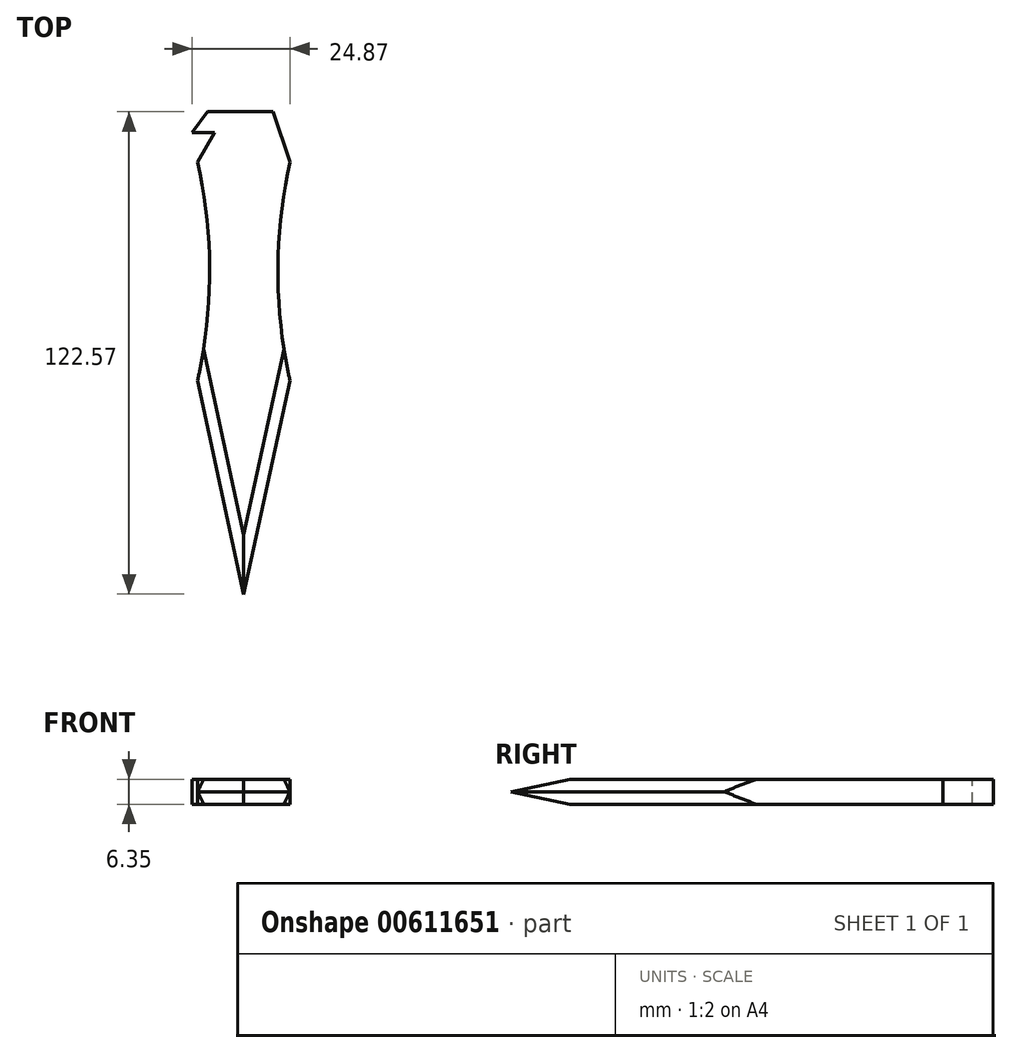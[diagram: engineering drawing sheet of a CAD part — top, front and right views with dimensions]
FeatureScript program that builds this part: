
annotation { "Feature Type Name" : "Feature", "Feature Type Description" : "" }
export const myFeature = defineFeature(function(context is Context, id is Id, definition is map)
    precondition{}
    {
        {
            var Q0;
            Q0=qCreatedBy(makeId("Top.planeOp"),FACE);
            var sketch = newSketch(context, id + "F0", { "sketchPlane" : qUnion([Q0])});
            skLineSegment(sketch, "E0", {"start": v(0, 0) * mm, "end": v(-11.74, 20.33) * mm});
            skLineSegment(sketch, "E1", {"start": v(-63.5, 109.99) * mm, "end": v(63.5, 109.99) * mm});
            skLineSegment(sketch, "E2", {"start": v(63.5, 109.99) * mm, "end": v(0, 0) * mm});
            skLineSegment(sketch, "E3", {"start": v(0, 0) * mm, "end": v(0, 19.44) * mm});
            skLineSegment(sketch, "E4", {"start": v(-60.33, 104.49) * mm, "end": v(-44.45, 109.99) * mm});
            skLineSegment(sketch, "E5.MirrorCS", {"start": v(60.33, 104.49) * mm, "end": v(44.45, 109.99) * mm});
            skLineSegment(sketch, "E6", {"start": v(-44.45, 109.99) * mm, "end": v(0, 63.5) * mm});
            skLineSegment(sketch, "E7", {"start": v(0, 63.5) * mm, "end": v(44.45, 109.99) * mm});
            skPoint(sketch, "E8", {"position": v(-11.74, 20.33) * mm});
            skPoint(sketch, "E9.MirrorP", {"position": v(11.74, 20.33) * mm});
            skLineSegment(sketch, "E10.MirrorCS", {"start": v(11.74, 20.33) * mm, "end": v(0, 29.52) * mm});
            skLineSegment(sketch, "E11.MirrorCS", {"start": v(0, 29.52) * mm, "end": v(-11.74, 20.33) * mm});
            skLineSegment(sketch, "E12", {"start": v(-49.19, 85.2) * mm, "end": v(-43.22, 86.8) * mm});
            skLineSegment(sketch, "E13", {"start": v(-43.22, 86.8) * mm, "end": v(-47.97, 83.1) * mm});
            skLineSegment(sketch, "E14", {"start": v(-35.1, 60.8) * mm, "end": v(-26.52, 63.68) * mm});
            skLineSegment(sketch, "E15", {"start": v(-26.52, 63.68) * mm, "end": v(-33.47, 57.97) * mm});
            skLineSegment(sketch, "E16.trimOffspring", {"start": v(-21.1, 36.55) * mm, "end": v(-33.47, 57.97) * mm});
            skLineSegment(sketch, "E17.trimOffspring", {"start": v(-35.1, 60.8) * mm, "end": v(-47.97, 83.1) * mm});
            skLineSegment(sketch, "E18.trimOffspring", {"start": v(-49.19, 85.2) * mm, "end": v(-63.5, 109.99) * mm});
            skLineSegment(sketch, "E19.MirrorCS", {"start": v(26.52, 63.68) * mm, "end": v(33.47, 57.97) * mm});
            skLineSegment(sketch, "E20.MirrorCS", {"start": v(35.1, 60.8) * mm, "end": v(26.52, 63.68) * mm});
            skLineSegment(sketch, "E21.MirrorCS", {"start": v(43.22, 86.8) * mm, "end": v(47.97, 83.1) * mm});
            skLineSegment(sketch, "E22.MirrorCS", {"start": v(49.19, 85.2) * mm, "end": v(43.22, 86.8) * mm});
            skLineSegment(sketch, "E23", {"start": v(-21.1, 36.55) * mm, "end": v(-11.74, 20.33) * mm});
            skSolve(sketch);
        }
        {
            var Q0;
            {var subQ3=sQuery(id+"F0.wireOp",EDGE,"E4");Q0=makeQuery(id+"F0.imprint","IMPRINT",FACE,{"disambiguationData":[TD([[makeQuery(id+"F0.imprint","IMPRINT",EDGE,{"derivedFrom":subQ3}),-1.0]])]});}
            extrude(context, id + "F1", {"entities" : qUnion([Q0]), "depth" : 6.35 * mm, "offsetDistance" : 25.4 * mm});
        }
        {
            var Q0;
            Q0=makeQuery(id+"F1.opExtrude","CAP_FACE",FACE,{"disambiguationData":[OSD([sQuery(id+"F0.wireOp",EDGE,"E2"),sQuery(id+"F0.wireOp",EDGE,"E4"),sQuery(id+"F0.wireOp",EDGE,"E5.MirrorCS"),sQuery(id+"F0.wireOp",EDGE,"E6"),sQuery(id+"F0.wireOp",EDGE,"E7"),sQuery(id+"F0.wireOp",EDGE,"E10.MirrorCS"),sQuery(id+"F0.wireOp",EDGE,"E11.MirrorCS"),sQuery(id+"F0.wireOp",EDGE,"E12"),sQuery(id+"F0.wireOp",EDGE,"E13"),sQuery(id+"F0.wireOp",EDGE,"E14"),sQuery(id+"F0.wireOp",EDGE,"E15"),sQuery(id+"F0.wireOp",EDGE,"E16.trimOffspring"),sQuery(id+"F0.wireOp",EDGE,"E17.trimOffspring"),sQuery(id+"F0.wireOp",EDGE,"E18.trimOffspring"),sQuery(id+"F0.wireOp",EDGE,"E19.MirrorCS"),sQuery(id+"F0.wireOp",EDGE,"E20.MirrorCS"),sQuery(id+"F0.wireOp",EDGE,"E21.MirrorCS"),sQuery(id+"F0.wireOp",EDGE,"E22.MirrorCS"),sQuery(id+"F0.wireOp",EDGE,"E23")])],"isStart":true});
            var sketch = newSketch(context, id + "F2", { "sketchPlane" : qUnion([Q0])});
            skPoint(sketch, "E24", {"position": v(11.74, -75.77) * mm});
            skPoint(sketch, "E25", {"position": v(-11.74, -75.77) * mm});
            skArc(sketch, "E26", {"start": v(11.74, -20.33) * mm, "mid": v(8.67, -48.05) * mm, "end": v(11.74, -75.77) * mm});
            skLineSegment(sketch, "E27", {"start": v(-11.74, -75.77) * mm, "end": v(-44.45, -109.99) * mm});
            skLineSegment(sketch, "E28", {"start": v(-44.45, -109.99) * mm, "end": v(-60.33, -104.49) * mm});
            skLineSegment(sketch, "E29", {"start": v(-60.33, -104.49) * mm, "end": v(-49.19, -85.2) * mm});
            skLineSegment(sketch, "E30", {"start": v(-49.19, -85.2) * mm, "end": v(-43.22, -86.8) * mm});
            skLineSegment(sketch, "E31", {"start": v(-43.22, -86.8) * mm, "end": v(-47.97, -83.1) * mm});
            skLineSegment(sketch, "E32", {"start": v(-47.97, -83.1) * mm, "end": v(-35.1, -60.8) * mm});
            skLineSegment(sketch, "E33", {"start": v(-35.1, -60.8) * mm, "end": v(-26.52, -63.68) * mm});
            skLineSegment(sketch, "E34", {"start": v(-26.52, -63.68) * mm, "end": v(-33.47, -57.97) * mm});
            skLineSegment(sketch, "E35", {"start": v(-33.47, -57.97) * mm, "end": v(-11.74, -20.33) * mm});
            skLineSegment(sketch, "E36", {"start": v(0, -29.52) * mm, "end": v(0, -16.78) * mm});
            skArc(sketch, "E37.MirrorCS", {"start": v(-11.74, -20.33) * mm, "mid": v(-8.67, -48.05) * mm, "end": v(-11.74, -75.77) * mm});
            skLineSegment(sketch, "E38.MirrorCS", {"start": v(11.74, -75.77) * mm, "end": v(44.45, -109.99) * mm});
            skLineSegment(sketch, "E39.MirrorCS", {"start": v(44.45, -109.99) * mm, "end": v(60.33, -104.49) * mm});
            skLineSegment(sketch, "E40.MirrorCS", {"start": v(60.33, -104.49) * mm, "end": v(49.19, -85.2) * mm});
            skLineSegment(sketch, "E41.MirrorCS", {"start": v(49.19, -85.2) * mm, "end": v(43.22, -86.8) * mm});
            skLineSegment(sketch, "E42.MirrorCS", {"start": v(43.22, -86.8) * mm, "end": v(47.97, -83.1) * mm});
            skLineSegment(sketch, "E43.MirrorCS", {"start": v(47.97, -83.1) * mm, "end": v(35.1, -60.8) * mm});
            skLineSegment(sketch, "E44.MirrorCS", {"start": v(26.52, -63.68) * mm, "end": v(33.47, -57.97) * mm});
            skLineSegment(sketch, "E45.MirrorCS", {"start": v(35.1, -60.8) * mm, "end": v(26.52, -63.68) * mm});
            skLineSegment(sketch, "E46.MirrorCS", {"start": v(33.47, -57.97) * mm, "end": v(11.74, -20.33) * mm});
            skSolve(sketch);
        }
        {
            var Q0;
            Q0=makeQuery(id+"F2.imprint","IMPRINT",FACE,{"disambiguationData":[TD([[makeQuery(id+"F2.imprint","IMPRINT",EDGE,{"derivedFrom":sQuery(id+"F2.wireOp",EDGE,"E27")}),1.0]])]});
            var Q1;
            Q1=makeQuery(id+"F2.imprint","IMPRINT",FACE,{"disambiguationData":[TD([[makeQuery(id+"F2.imprint","IMPRINT",EDGE,{"derivedFrom":sQuery(id+"F2.wireOp",EDGE,"E26")}),1.0]])]});
            extrude(context, id + "F3", {"entities" : qUnion([Q0, Q1]), "operationType" : NewBodyOperationType.REMOVE, "oppositeDirection" : true, "depth" : 25.4 * mm, "offsetDistance" : 25.4 * mm});
        }
        {
            var Q0;
            Q0=makeQuery(id+"F1.opExtrude","CAP_FACE",FACE,{"disambiguationData":[OSD([sQuery(id+"F0.wireOp",EDGE,"E2"),sQuery(id+"F0.wireOp",EDGE,"E4"),sQuery(id+"F0.wireOp",EDGE,"E5.MirrorCS"),sQuery(id+"F0.wireOp",EDGE,"E6"),sQuery(id+"F0.wireOp",EDGE,"E7"),sQuery(id+"F0.wireOp",EDGE,"E10.MirrorCS"),sQuery(id+"F0.wireOp",EDGE,"E11.MirrorCS"),sQuery(id+"F0.wireOp",EDGE,"E12"),sQuery(id+"F0.wireOp",EDGE,"E13"),sQuery(id+"F0.wireOp",EDGE,"E14"),sQuery(id+"F0.wireOp",EDGE,"E15"),sQuery(id+"F0.wireOp",EDGE,"E16.trimOffspring"),sQuery(id+"F0.wireOp",EDGE,"E17.trimOffspring"),sQuery(id+"F0.wireOp",EDGE,"E18.trimOffspring"),sQuery(id+"F0.wireOp",EDGE,"E19.MirrorCS"),sQuery(id+"F0.wireOp",EDGE,"E20.MirrorCS"),sQuery(id+"F0.wireOp",EDGE,"E21.MirrorCS"),sQuery(id+"F0.wireOp",EDGE,"E22.MirrorCS"),sQuery(id+"F0.wireOp",EDGE,"E23")])],"isStart":false});
            var sketch = newSketch(context, id + "F4", { "sketchPlane" : qUnion([Q0])});
            skLineSegment(sketch, "E47", {"start": v(-11.74, 75.77) * mm, "end": v(-7.43, 83.29) * mm});
            skLineSegment(sketch, "E48", {"start": v(-13.13, 83.29) * mm, "end": v(-9.22, 88.6) * mm});
            skLineSegment(sketch, "E49", {"start": v(-9.22, 88.6) * mm, "end": v(7.42, 88.6) * mm});
            skLineSegment(sketch, "E50", {"start": v(7.42, 88.6) * mm, "end": v(11.74, 75.77) * mm});
            skLineSegment(sketch, "E51", {"start": v(-13.13, 83.29) * mm, "end": v(-7.43, 83.29) * mm});
            skLineSegment(sketch, "E52", {"start": v(-11.74, 75.77) * mm, "end": v(0, 63.5) * mm});
            skLineSegment(sketch, "E53", {"start": v(0, 63.5) * mm, "end": v(11.74, 75.77) * mm});
            skLineSegment(sketch, "E54", {"start": v(-11.74, 20.33) * mm, "end": v(0, 29.52) * mm});
            skLineSegment(sketch, "E55", {"start": v(11.74, 20.33) * mm, "end": v(0, 29.52) * mm});
            skLineSegment(sketch, "E56", {"start": v(-11.74, 20.33) * mm, "end": v(0, -33.98) * mm});
            skLineSegment(sketch, "E57", {"start": v(0, -33.98) * mm, "end": v(11.74, 20.33) * mm});
            skSolve(sketch);
        }
        {
            var Q0;
            Q0=makeQuery(id+"F4.imprint","IMPRINT",FACE,{"disambiguationData":[TD([[makeQuery(id+"F4.imprint","IMPRINT",EDGE,{"derivedFrom":sQuery(id+"F4.wireOp",EDGE,"E47")}),-1.0]])]});
            var Q1;
            Q1=makeQuery(id+"F4.imprint","IMPRINT",FACE,{"disambiguationData":[TD([[makeQuery(id+"F4.imprint","IMPRINT",EDGE,{"derivedFrom":sQuery(id+"F4.wireOp",EDGE,"E54")}),1.0]])]});
            extrude(context, id + "F5", {"entities" : qUnion([Q0, Q1]), "operationType" : NewBodyOperationType.ADD, "oppositeDirection" : true, "depth" : 6.35 * mm, "offsetDistance" : 25.4 * mm});
        }
        {
            var Q0;
            Q0=makeQuery(id+"F5.opExtrude","CAP_EDGE",EDGE,{"disambiguationData":[OSD([sQuery(id+"F4.wireOp",EDGE,"E57")])],"isStart":true});
            var Q1;
            Q1=makeQuery(id+"F5.opExtrude","CAP_EDGE",EDGE,{"disambiguationData":[OSD([sQuery(id+"F4.wireOp",EDGE,"E56")])],"isStart":true});
            var Q2;
            Q2=makeQuery(id+"F5.opExtrude","CAP_EDGE",EDGE,{"disambiguationData":[OSD([sQuery(id+"F4.wireOp",EDGE,"E57")])],"isStart":false});
            var Q3;
            Q3=makeQuery(id+"F5.opExtrude","CAP_EDGE",EDGE,{"disambiguationData":[OSD([sQuery(id+"F4.wireOp",EDGE,"E56")])],"isStart":false});
            chamfer(context, id + "F6", {"entities" : qUnion([Q0, Q1, Q2, Q3]), "width" : 3.17 * mm, "tangentPropagation" : true});
        }
    });
